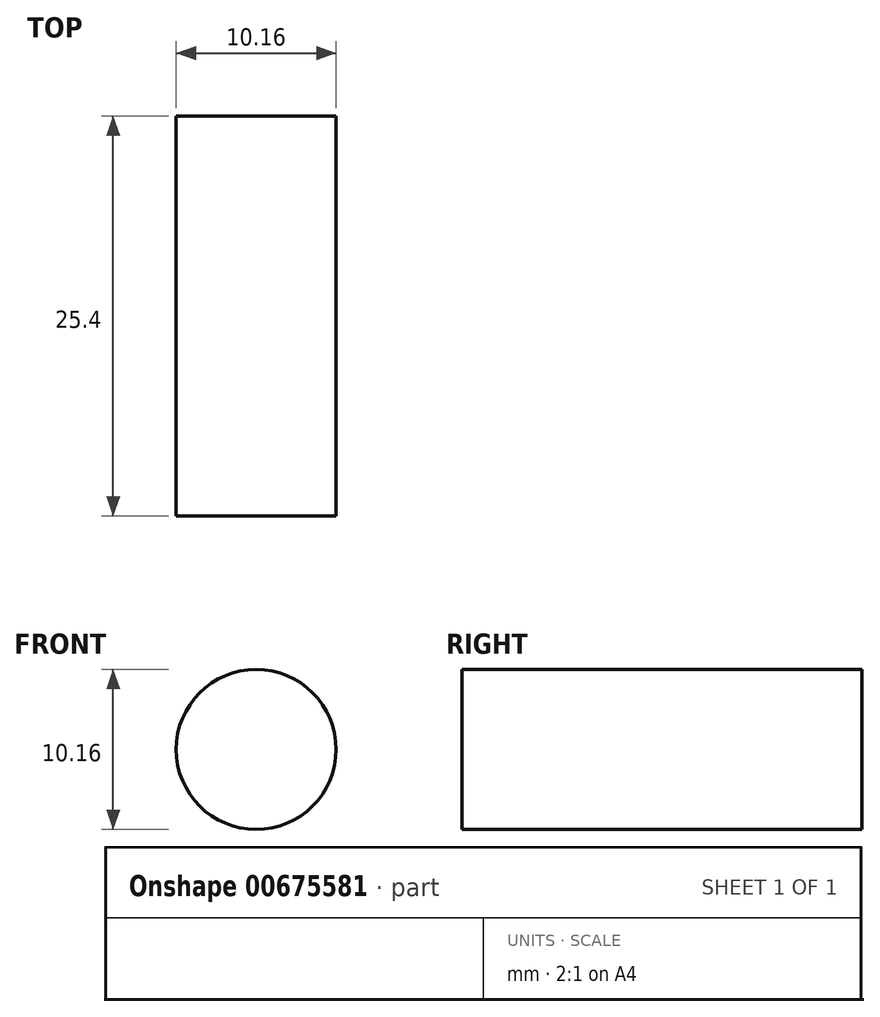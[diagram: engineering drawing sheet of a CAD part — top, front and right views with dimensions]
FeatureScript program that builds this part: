
annotation { "Feature Type Name" : "Feature", "Feature Type Description" : "" }
export const myFeature = defineFeature(function(context is Context, id is Id, definition is map)
    precondition{}
    {
        {
            var Q0;
            Q0=qCreatedBy(makeId("Front.planeOp"),FACE);
            var sketch = newSketch(context, id + "F0", { "sketchPlane" : qUnion([Q0])});
            skCircle(sketch, "E0", {"center": v(0, 0) * mm, "radius": 5.08 * mm});
            skSolve(sketch);
        }
        {
            var Q0;
            Q0 = qSketchRegion(id + "F0", true);
            extrude(context, id + "F1", {"entities" : qUnion([Q0]), "depth" : 25.4 * mm, "offsetDistance" : 25.4 * mm});
        }
    });
